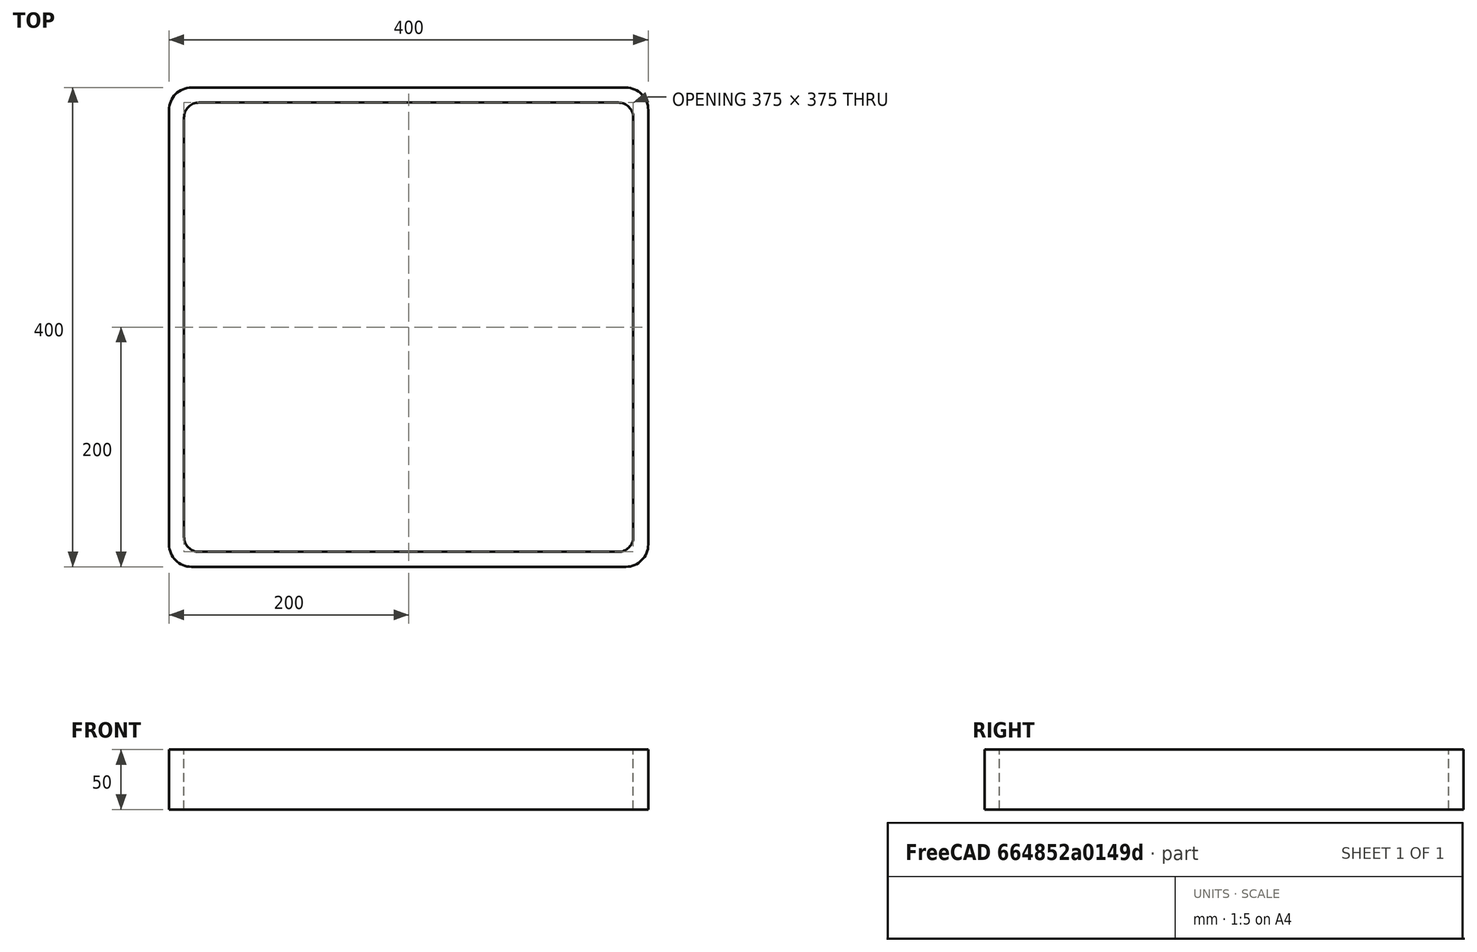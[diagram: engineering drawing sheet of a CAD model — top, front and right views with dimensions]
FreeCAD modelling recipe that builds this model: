
FCSTD DOCUMENT  (FreeCAD 0.15R4671 (Git))
Label: Square hollow section 400x400x12.5 EN10219 S235JRH
License: All rights reserved
LicenseURL: http://en.wikipedia.org/wiki/All_rights_reserved
objects: Sketcher::SketchObject×1, Part::Extrusion×1
note: 2 computed .brp shape members not serialized (recipe doc carries the construction recipe); baked Part::Feature solids carry a one-line shape summary decoded from their .brp

FEATURE [Sketcher::SketchObject] Sketch
  sketch-geometry (16):
    g0: LineSegment StartX=-175 StartY=187.5 StartZ=0 EndX=175 EndY=187.5 EndZ=0
    g1: LineSegment StartX=187.5 StartY=175 StartZ=0 EndX=187.5 EndY=-175 EndZ=0
    g2: LineSegment StartX=175 StartY=-187.5 StartZ=0 EndX=-175 EndY=-187.5 EndZ=0
    g3: LineSegment StartX=-187.5 StartY=-175 StartZ=0 EndX=-187.5 EndY=175 EndZ=0
    g4: LineSegment StartX=-181.25 StartY=200 StartZ=0 EndX=181.25 EndY=200 EndZ=0
    g5: LineSegment StartX=200 StartY=181.25 StartZ=0 EndX=200 EndY=-181.25 EndZ=0
    g6: LineSegment StartX=181.25 StartY=-200 StartZ=0 EndX=-181.25 EndY=-200 EndZ=0
    g7: LineSegment StartX=-200 StartY=-181.25 StartZ=0 EndX=-200 EndY=181.25 EndZ=0
    g8: ArcOfCircle CenterX=-175 CenterY=175 CenterZ=0 NormalX=0 NormalY=0 NormalZ=1 Radius=12.5 StartAngle=1.5708 EndAngle=3.14159
    g9: ArcOfCircle CenterX=175 CenterY=175 CenterZ=0 NormalX=0 NormalY=0 NormalZ=1 Radius=12.5 StartAngle=0 EndAngle=1.5708
    g10: ArcOfCircle CenterX=175 CenterY=-175 CenterZ=0 NormalX=0 NormalY=0 NormalZ=1 Radius=12.5 StartAngle=4.71239 EndAngle=6.28319
    g11: ArcOfCircle CenterX=-175 CenterY=-175 CenterZ=0 NormalX=0 NormalY=0 NormalZ=1 Radius=12.5 StartAngle=3.14159 EndAngle=4.71239
    g12: ArcOfCircle CenterX=181.25 CenterY=181.25 CenterZ=0 NormalX=0 NormalY=0 NormalZ=1 Radius=18.75 StartAngle=0 EndAngle=1.5708
    g13: ArcOfCircle CenterX=181.25 CenterY=-181.25 CenterZ=0 NormalX=0 NormalY=0 NormalZ=1 Radius=18.75 StartAngle=4.71239 EndAngle=6.28319
    g14: ArcOfCircle CenterX=-181.25 CenterY=-181.25 CenterZ=0 NormalX=0 NormalY=0 NormalZ=1 Radius=18.75 StartAngle=3.14159 EndAngle=4.71239
    g15: ArcOfCircle CenterX=-181.25 CenterY=181.25 CenterZ=0 NormalX=0 NormalY=0 NormalZ=1 Radius=18.75 StartAngle=1.5708 EndAngle=3.14159
  constraints (36):
    c: Horizontal(g2)
    c: Vertical(g3)
    c: Horizontal(g6)
    c: Vertical(g7)
    c: Tangent(g3,g8) = 1.5708
    c: Tangent(g0,g8) = 1.5708
    c: Tangent(g0,g9) = 1.5708
    c: Tangent(g1,g9) = 1.5708
    c: Tangent(g1,g10) = 1.5708
    c: Tangent(g2,g10) = 1.5708
    c: Tangent(g2,g11) = 1.5708
    c: Tangent(g3,g11) = 1.5708
    c: Tangent(g4,g12) = 1.5708
    c: Tangent(g5,g12) = 1.5708
    c: Tangent(g5,g13) = 1.5708
    c: Tangent(g6,g13) = 1.5708
    c: Tangent(g6,g14) = 1.5708
    c: Tangent(g7,g14) = 1.5708
    c: Tangent(g7,g15) = 1.5708
    c: Tangent(g4,g15) = 1.5708
    c: Equal(g9,g8)
    c: Equal(g9,g11)
    c: Equal(g9,g10)
    c: Equal(g12,g15)
    c: Equal(g12,g14)
    c: Equal(g12,g13)
    c: Symmetric(g4,g6,g-1)
    c: Symmetric(g7,g5,g-2)
    c: DistanceY(g4,g6) = -400
    c: DistanceX(g7,g5) = 400
    c: Symmetric(g3,g1,g-2)
    c: Symmetric(g0,g2,g-1)
    c: DistanceY(g0,g4) = 12.5
    c: DistanceX(g5,g1) = -12.5
    c: Radius(g9) = 12.5
    c: Radius(g12) = 18.75
FEATURE [Part::Extrusion] Extrude  label="Square hollow section 400x400x12.5 EN10219 S235JRH"
  Base = -> Sketch
  Dir = (0,0,50)
  Solid = true
